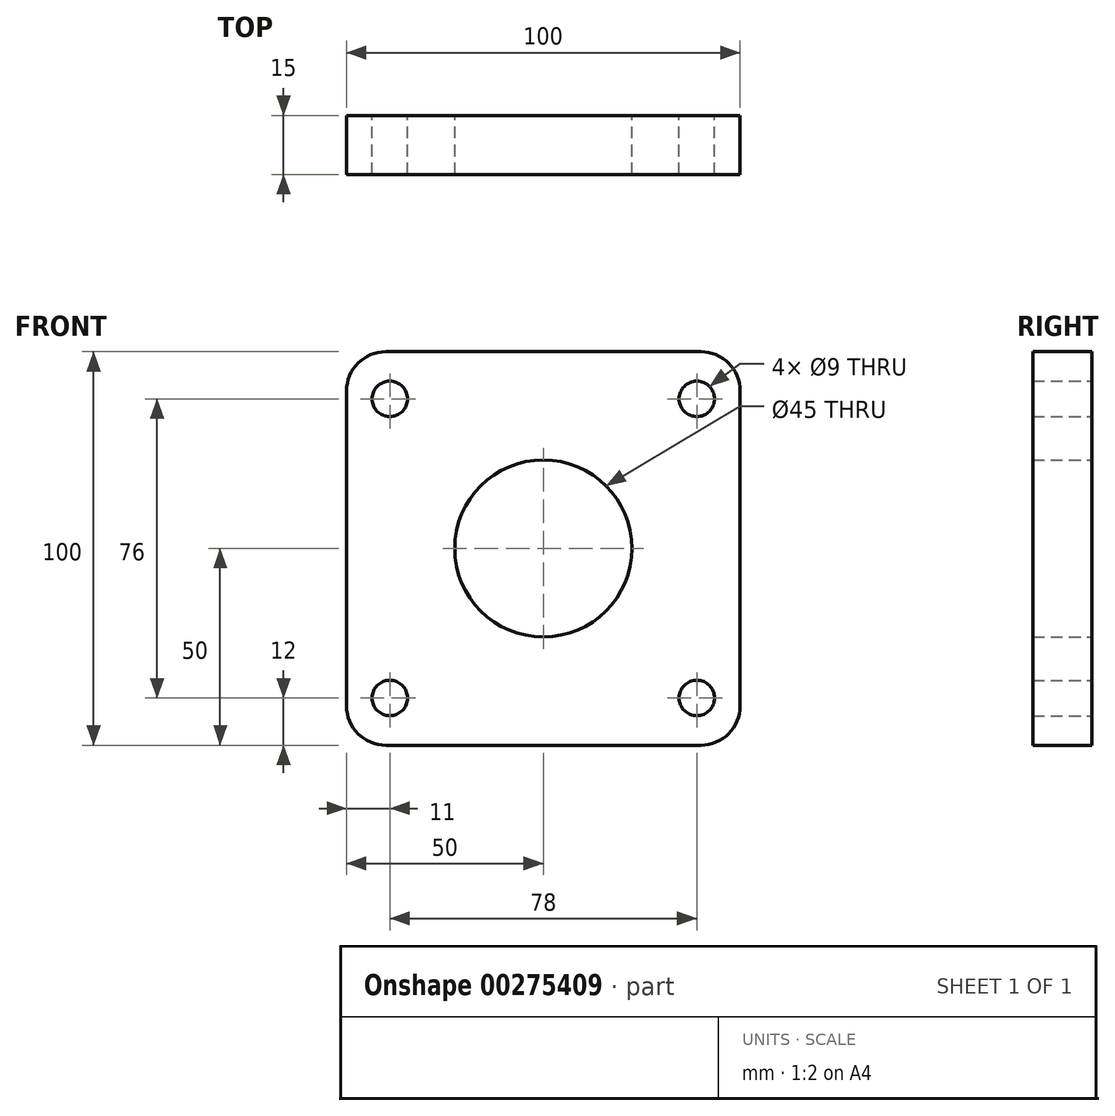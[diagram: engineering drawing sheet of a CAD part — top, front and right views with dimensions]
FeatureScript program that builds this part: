
annotation { "Feature Type Name" : "Feature", "Feature Type Description" : "" }
export const myFeature = defineFeature(function(context is Context, id is Id, definition is map)
    precondition{}
    {
        {
            var Q0;
            Q0=qCreatedBy(makeId("Front.planeOp"),FACE);
            var sketch = newSketch(context, id + "F0", { "sketchPlane" : qUnion([Q0])});
            skLineSegment(sketch, "E0.bottom", {"start": v(-40, 50) * mm, "end": v(40, 50) * mm});
            skLineSegment(sketch, "E0.top", {"start": v(-40, -50) * mm, "end": v(40, -50) * mm});
            skLineSegment(sketch, "E0.left", {"start": v(-50, 40) * mm, "end": v(-50, -40) * mm});
            skLineSegment(sketch, "E0.right", {"start": v(50, 40) * mm, "end": v(50, -40) * mm});
            skPoint(sketch, "E1.visualSharp", {"position": v(-50, 50) * mm});
            skArc(sketch, "E1.filletArc", {"start": v(-40, 50) * mm, "mid": v(-47.07, 47.07) * mm, "end": v(-50, 40) * mm});
            skPoint(sketch, "E2.visualSharp", {"position": v(50, 50) * mm});
            skArc(sketch, "E2.filletArc", {"start": v(50, 40) * mm, "mid": v(47.07, 47.07) * mm, "end": v(40, 50) * mm});
            skPoint(sketch, "E3.visualSharp", {"position": v(50, -50) * mm});
            skArc(sketch, "E3.filletArc", {"start": v(40, -50) * mm, "mid": v(47.07, -47.07) * mm, "end": v(50, -40) * mm});
            skPoint(sketch, "E4.visualSharp", {"position": v(-50, -50) * mm});
            skArc(sketch, "E4.filletArc", {"start": v(-50, -40) * mm, "mid": v(-47.07, -47.07) * mm, "end": v(-40, -50) * mm});
            skCircle(sketch, "E5", {"center": v(0, 0) * mm, "radius": 22.5 * mm});
            skCircle(sketch, "E6", {"center": v(-39, 38) * mm, "radius": 4.5 * mm});
            skCircle(sketch, "E7", {"center": v(-39, -38) * mm, "radius": 4.5 * mm});
            skCircle(sketch, "E8", {"center": v(39, -38) * mm, "radius": 4.5 * mm});
            skCircle(sketch, "E9", {"center": v(39, 38) * mm, "radius": 4.5 * mm});
            skSolve(sketch);
        }
        {
            var Q0;
            Q0=makeQuery(id+"F0.imprint","IMPRINT",FACE,{"disambiguationData":[TD([[makeQuery(id+"F0.imprint","IMPRINT",EDGE,{"derivedFrom":sQuery(id+"F0.wireOp",EDGE,"E0.bottom")}),-1.0]])]});
            extrude(context, id + "F1", {"entities" : qUnion([Q0]), "depth" : 15 * mm});
        }
    });
